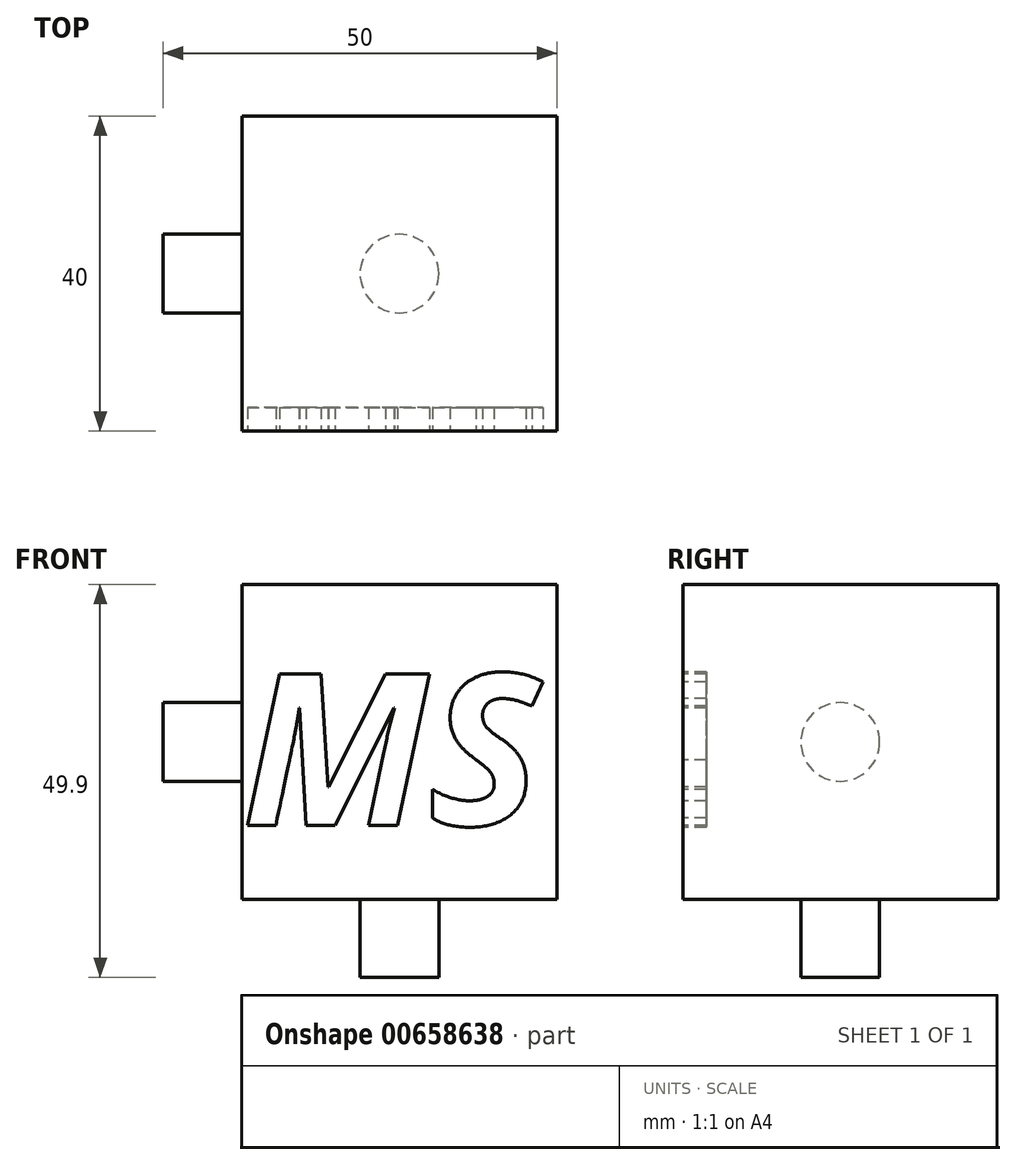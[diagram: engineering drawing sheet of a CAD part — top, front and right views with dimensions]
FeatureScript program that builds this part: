
annotation { "Feature Type Name" : "Feature", "Feature Type Description" : "" }
export const myFeature = defineFeature(function(context is Context, id is Id, definition is map)
    precondition{}
    {
        {
            var Q0;
            Q0=qCreatedBy(makeId("Front.planeOp"),FACE);
            var sketch = newSketch(context, id + "F0", { "sketchPlane" : qUnion([Q0])});
            skLineSegment(sketch, "E0", {"start": v(0, 0) * mm, "end": v(0, -40) * mm});
            skLineSegment(sketch, "E1", {"start": v(0, -40) * mm, "end": v(40, -40) * mm});
            skLineSegment(sketch, "E2", {"start": v(40, -40) * mm, "end": v(40, 0) * mm});
            skLineSegment(sketch, "E3", {"start": v(40, 0) * mm, "end": v(0, 0) * mm});
            skSolve(sketch);
        }
        {
            var Q0;
            Q0=makeQuery(id+"F0.imprint","IMPRINT",FACE,{"disambiguationData":[TD([[makeQuery(id+"F0.imprint","IMPRINT",EDGE,{"derivedFrom":sQuery(id+"F0.wireOp",EDGE,"E0")}),1.0]])]});
            extrude(context, id + "F1", {"entities" : qUnion([Q0]), "depth" : 40 * mm, "offsetDistance" : 25 * mm});
        }
        {
            var Q0;
            Q0=qCreatedBy(makeId("Right.planeOp"),FACE);
            var sketch = newSketch(context, id + "F2", { "sketchPlane" : qUnion([Q0])});
            skCircle(sketch, "E4", {"center": v(-20, -20) * mm, "radius": 5 * mm});
            skSolve(sketch);
        }
        {
            var Q0;
            Q0=makeQuery(id+"F2.imprint","IMPRINT",FACE,{"disambiguationData":[TD([[makeQuery(id+"F2.imprint","IMPRINT",EDGE,{"derivedFrom":sQuery(id+"F2.wireOp",EDGE,"E4")}),1.0]])]});
            extrude(context, id + "F3", {"entities" : qUnion([Q0]), "operationType" : NewBodyOperationType.ADD, "oppositeDirection" : true, "depth" : 10 * mm, "offsetDistance" : 25 * mm});
        }
        {
            var Q0;
            Q0=qCreatedBy(makeId("Right.planeOp"),FACE);
            var sketch = newSketch(context, id + "F4", { "sketchPlane" : qUnion([Q0])});
            skCircle(sketch, "E5", {"center": v(-20, -20) * mm, "radius": 5 * mm});
            skSolve(sketch);
        }
        {
            var Q0;
            Q0 = qSketchRegion(id + "F4", true);
            extrude(context, id + "F5", {"entities" : qUnion([Q0]), "operationType" : NewBodyOperationType.ADD, "oppositeDirection" : true, "depth" : 10 * mm, "offsetDistance" : 25 * mm});
        }
        {
            var Q0;
            Q0=qCreatedBy(makeId("Right.planeOp"),FACE);
            var sketch = newSketch(context, id + "F6", { "sketchPlane" : qUnion([Q0])});
            skCircle(sketch, "E6", {"center": v(-20, -20) * mm, "radius": 5 * mm});
            skSolve(sketch);
        }
        {
            var Q0;
            Q0 = qSketchRegion(id + "F6", true);
            extrude(context, id + "F7", {"entities" : qUnion([Q0]), "operationType" : NewBodyOperationType.ADD, "oppositeDirection" : true, "depth" : 9.9 * mm, "offsetDistance" : 25 * mm});
        }
        {
            var Q0;
            Q0=makeQuery(id+"F1.opExtrude","SWEPT_FACE",FACE,{"disambiguationData":[OSD([sQuery(id+"F0.wireOp",EDGE,"E1")])]});
            var sketch = newSketch(context, id + "F8", { "sketchPlane" : qUnion([Q0])});
            skCircle(sketch, "E7", {"center": v(20, 20) * mm, "radius": 5 * mm});
            skSolve(sketch);
        }
        {
            var Q0;
            Q0=makeQuery(id+"F8.imprint","IMPRINT",FACE,{"disambiguationData":[TD([[makeQuery(id+"F8.imprint","IMPRINT",EDGE,{"derivedFrom":sQuery(id+"F8.wireOp",EDGE,"E7")}),1.0]])]});
            extrude(context, id + "F9", {"entities" : qUnion([Q0]), "operationType" : NewBodyOperationType.ADD, "depth" : 9.9 * mm, "offsetDistance" : 25 * mm});
        }
        {
            var Q0;
            Q0=makeQuery(id+"F1.opExtrude","CAP_FACE",FACE,{"disambiguationData":[OSD([sQuery(id+"F0.wireOp",EDGE,"E0"),sQuery(id+"F0.wireOp",EDGE,"E1"),sQuery(id+"F0.wireOp",EDGE,"E2"),sQuery(id+"F0.wireOp",EDGE,"E3")])],"isStart":false});
            var sketch = newSketch(context, id + "F10", { "sketchPlane" : qUnion([Q0])});
            skText(sketch, "E8", { "text": "MS", "fontName": "OpenSans-BoldItalic.ttf"});
            const initialGuessF10  = {"E8": [0, -0.03057, 1, 0, 0.01937]};
            skSetInitialGuess(sketch, initialGuessF10);
            skSolve(sketch);
        }
        {
            var Q0;
            Q0 = qSketchRegion(id + "F10", true);
            extrude(context, id + "F11", {"entities" : qUnion([Q0]), "operationType" : NewBodyOperationType.REMOVE, "oppositeDirection" : true, "depth" : 3 * mm, "offsetDistance" : 25 * mm});
        }
    });
